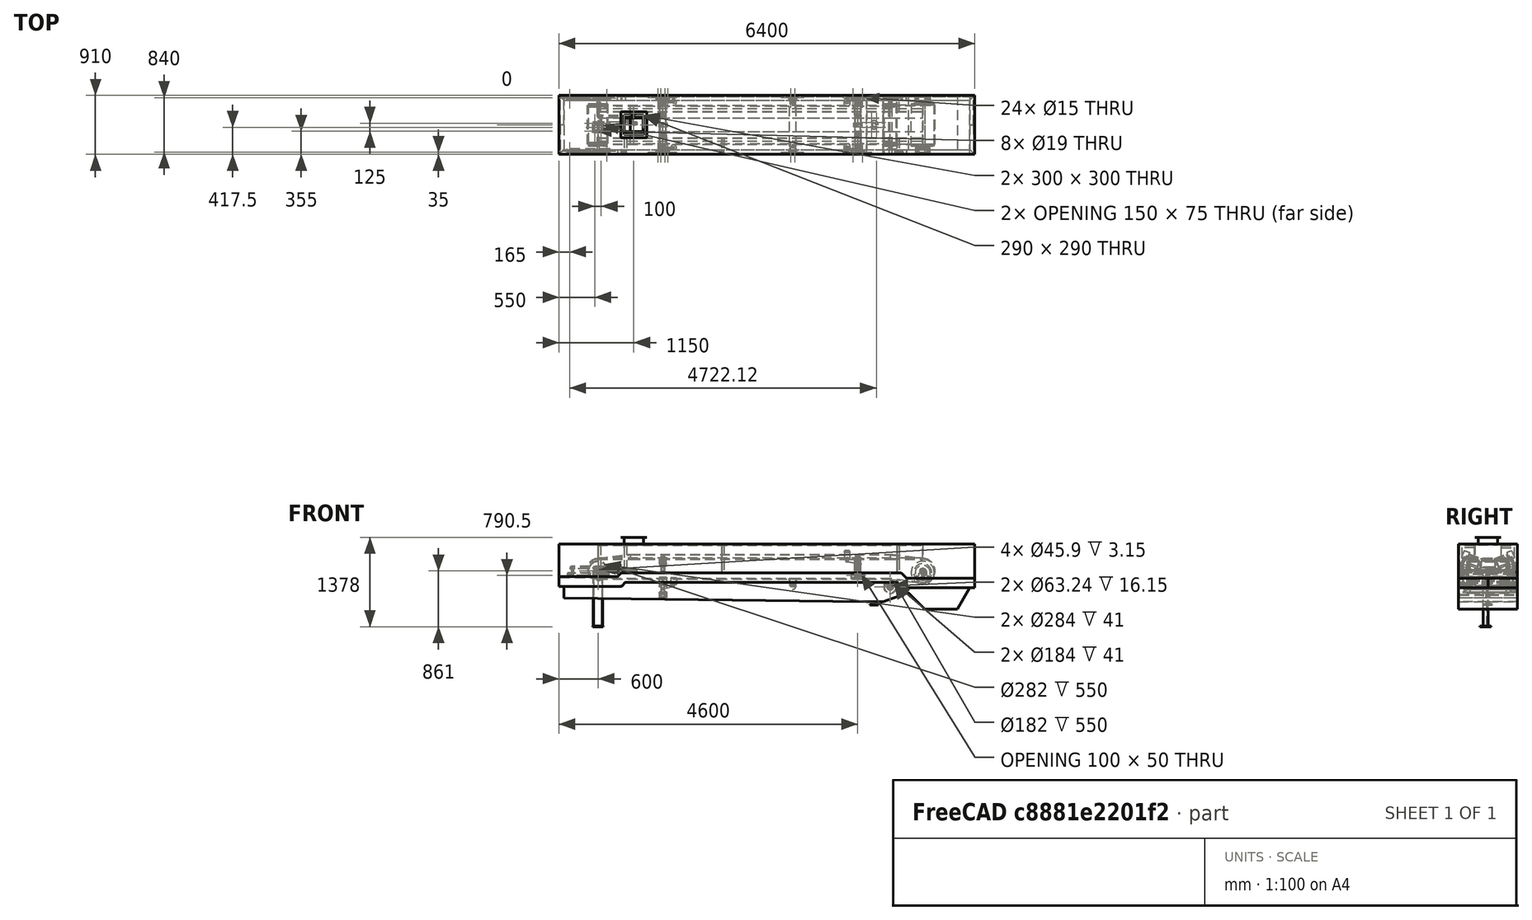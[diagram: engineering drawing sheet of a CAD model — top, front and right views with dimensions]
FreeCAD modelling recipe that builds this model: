
FCSTD DOCUMENT  (FreeCAD 0.21R33771 (Git))
Label: BeltCv600BAssy
License: All rights reserved
LicenseURL: http://en.wikipedia.org/wiki/All_rights_reserved
objects: Sketcher::SketchObject×23, Part::Extrusion×18, App::Part×18, Part::FeaturePython×15, Part::MultiFuse×10, Part::Feature×9, Part::Sweep×5, Part::Mirroring×4, Part::Thickness×3, Spreadsheet::Sheet×2, Part::Cut×2, Part::Compound×1, TechDraw::DrawSVGTemplate×1, TechDraw::DrawViewPart×1, TechDraw::DrawViewDimension×1, TechDraw::DrawPage×1
note: 89 computed .brp shape members not serialized (recipe doc carries the construction recipe); baked Part::Feature solids carry a one-line shape summary decoded from their .brp

FEATURE [Spreadsheet::Sheet] Spreadsheet
  cells = C1='tailPulleyHIght Ht; D1='Inclination k(degree); A2='CenterDistance C0; B2(C0)=5000; C2(Ht)=1000; D2(k)=10; A3='BeltWidth B0; B3(B0)=600; C3=400; D3=450; E3=500; F3=600; G3=700; H3=750; I3=800; J3=900; K3=1000; A4='Belt b1; B4(b1)=210; C4=145; D4=165; E4=180; F4=210; G4=250; H4=265; I4=280; J4=315; K4=345; A5='Belt b2; B5(b2)=195; C5==(C3 - C4) / 2; D5==(D3 - D4) / 2; E5==(E3 - E4) / 2; F5==(F3 - F4) / 2; G5==(G3 - G4) / 2; H5==(H3 - H4) / 2; I5==(I3 - I4) / 2; J5==(J3 - J4) / 2; K5==(K3 - K4) / 2; A6='BeltThickness t0; B6(t0)=10; C6=10; D6=10; E6=10; F6=10; G6=10; H6=10; I6=10; J6=10; K6=10; A7='HeadPullyDia D0; B7(D0)=360; C7=300; D7=300; E7=360; F7=360; G7=360; H7=460; I7=460; J7=520; K7=520; A8='TailPullyDia d1; B8(d1)=300; C8=260; D8=260; E8=300; F8=300; G8=300; H8=390; I8=390; J8=440; K8=440; A9='SnapPullyDia d2; B9(d2)=200; C9=200; D9=200; E9=200; F9=200; G9=200; H9=200; I9=200; J9=200; K9=200; A10='SnapPully Ls; B10(Ls)=500; C10=400; D10=400; E10=400; F10=500; G10=500; H10=500; I10=500; J10=500; K10=500; A11='SnapPully h0; B11(h0)=180; C11=180; D11=180; E11=160; F11=180; G11=180; H11=180; I11=180; J11=180; K11=180; A12='hontaihaba W; B12=910; C12=710; D12=760; E12=810; F12=910; G12=910; H12=910; I12=910; J12=910; K12=910; A13='hontai _h; B13=103.5; C13=103.5; D13=103.5; E13=103.5; F13=103.5; G13=103.5; H13=103.5; I13=103.5; J13=103.5; K13=103.5; A14='hontai_z; B14=16; C14=16; D14=16; E14=16; F14=16; G14=16; H14=16; I14=16; J14=16; K14=16; A15='takeup_x; B15=-403.47; C15=-403.47; D15=-403.47; E15=-403.47; F15=-403.47; G15=-403.47; H15=-403.47; I15=-403.47; J15=-403.47; K15=-403.47; A16='takeup_y; B16=-410; C16=-362.8; D16=-362.8; E16=-362.8; F16=-410; G16=-410; H16=-410; I16=-410; J16=-410; K16=-410; A17='takeup_z; B17=-57; C17=-87; D17=-87; E17=-87; F17=-57; G17=-57; H17=-57; I17=-57; J17=-57; K17=-57; A18='carrierPitch  cp; B18=1000; A19='returnPitch rp; B19=1500
FEATURE [Part::FeaturePython] CPM2_4145  # WARN: FeaturePython — macro-defined, semantics opaque (R4)
  A = 650
  B1 = 500
  B2 = 600
  C = 70
  D = 360
  D1 = 356
  D2 = 228
  D3 = 278
  E = 170
  F = 0
  G1 = 30
  G2 = 30
  H = 33
  L = 863
  M = 210
  N1 = 60
  N2 = 60
  P = 75
  Placement = pos=(5000,0,-30) rot=(0,0,1;1.5708rad)
  R = 20
  a = 11
  b = 11
  d = 18
  key = 5
  expr: .Placement.Base.x = Spreadsheet.C0
FEATURE [Sketcher::SketchObject] Sketch007
  FullyConstrained = true
  MapMode = 5
  Placement = pos=(0,0,14) rot=(1,0,0;1.5708rad)
  expr: Constraints[11] = Spreadsheet.C0 + 1000
  sketch-geometry (5):
    g0: LineSegment StartX=-600 StartY=-99 StartZ=0 EndX=250 EndY=-99 EndZ=0
    g1: LineSegment StartX=250 StartY=-99 StartZ=0 EndX=309 EndY=-40 EndZ=0
    g2: LineSegment StartX=309 StartY=-40 StartZ=0 EndX=4728 EndY=-40 EndZ=0
    g3: LineSegment StartX=4728 StartY=-40 StartZ=0 EndX=4800 EndY=-112 EndZ=0
    g4: LineSegment StartX=4800 StartY=-112 StartZ=0 EndX=6000 EndY=-112 EndZ=0
  constraints (16):
    c: Horizontal(g0)
    c: Coincident(g0,g1)
    c: Coincident(g1,g2)
    c: Horizontal(g2)
    c: Coincident(g2,g3)
    c: Coincident(g3,g4)
    c: Horizontal(g4)
    c: DistanceX(g0,g-1) = 600
    c: Angle(g1,g0) = 2.35619
    c: DistanceX(g-1,g0) = 250
    c: Angle(g4,g3) = 2.35619
    c: DistanceX(g-1,g4) = 6000
    c: DistanceX(g4,g4) = 1200
    c: DistanceY(g0,g-1) = 99
    c: DistanceY(g0,g1) = 59
    c: DistanceY(g-1,g3) = -112
FEATURE [Part::Feature] ChannelSteel001
  Placement = pos=(-600,-2.2e-14,-239) rot=(0,0,1;0rad)
  shape: bbox 2e-07 x 75 x 150 mm, 0 faces, 0 solids (baked)
FEATURE [Part::Feature] Carrier_600
  Placement = pos=(1000,-445,15) rot=(0,0,1;1.5708rad)
  shape: bbox 200 x 890 x 266 mm, 116 faces, 3 solids (baked)
FEATURE [Part::FeaturePython] Array  label="carrier"  # Draft array (typed FeaturePython)
  AlwaysSyncPlacement = false
  Angle = 360
  ArrayType = 0
  Axis = (0,0,1)
  Base = -> Carrier_600
  Center = (0,0,0)
  Count = 3
  ExpandArray = false
  Fuse = false
  IntervalAxis = (0,0,0)
  IntervalX = (1000,0,0)
  IntervalY = (0,100,0)
  IntervalZ = (0,0,100)
  NumberCircles = 3
  NumberPolar = 5
  NumberX = 3
  NumberY = 1
  NumberZ = 1
  PlacementList = 3 placements: arithmetic series from (1000,-445,15) step (1000,0,0) to (3000,-445,15)
  RadialDistance = 50
  ScaleList = (3) [(1,1,1),(1,1,1),(1,1,1)]
  Symmetry = 1
  TangentialDistance = 25
  expr: NumberX = Spreadsheet.C0 / Spreadsheet.B18 - 2
FEATURE [Part::FeaturePython] BendPulley  # WARN: FeaturePython — macro-defined, semantics opaque (R4)
  A = 50
  B = 103.5
  C = 700
  D = 200
  E = 0
  L = 650
  Placement = pos=(4500,1.79e-13,-250.18) rot=(0,0,-1;1.5708rad)
  d1 = 50
  d2 = 45
  d3 = 0
  t1 = 9
  t2 = 9
  t3 = 8
  t4 = 8
  expr: .Placement.Base.x = Spreadsheet.C0 - 500
FEATURE [Part::Feature] Part__Feature003  label="UCP208FC"
  Placement = pos=(4500,-410.5,-250.18) rot=(0,0.707107,-0.707107;3.14159rad)
  shape: bbox 184 x 86 x 106.1 mm, 117 faces (baked)
  expr: .Placement.Base.x = Spreadsheet.C0 - 500
FEATURE [Part::Feature] Self_Aligning_Carrier_600
  Placement = pos=(4000,1.108e-12,-38) rot=(0,0,-1;1.5708rad)
  shape: bbox 308 x 890 x 416.2 mm, 193 faces, 4 solids (baked)
  expr: .Placement.Base.x = Spreadsheet.C0 - 1000
FEATURE [Part::Feature] Self_Aligning_Return_600
  Placement = pos=(1000,0,-210) rot=(0,0,1;1.5708rad)
  shape: bbox 268 x 890 x 310 mm, 134 faces, 5 solids (baked)
FEATURE [Part::Feature] Return_600
  Placement = pos=(3000,7.84e-13,-234) rot=(0,0,1;1.5708rad)
  shape: bbox 110 x 890 x 159.5 mm, 37 faces (baked)
FEATURE [Part::FeaturePython] Array001  label="returnArray"  # Draft array (typed FeaturePython)
  AlwaysSyncPlacement = false
  Angle = 360
  ArrayType = 0
  Axis = (0,0,1)
  Base = -> Return_600
  Center = (0,0,0)
  Count = 1
  ExpandArray = false
  Fuse = false
  IntervalAxis = (0,0,0)
  IntervalX = (2000,0,0)
  IntervalY = (0,100,0)
  IntervalZ = (0,0,100)
  NumberCircles = 3
  NumberPolar = 5
  NumberX = 1
  NumberY = 1
  NumberZ = 1
  Placement = pos=(0,0,14) rot=(0,0,1;0rad)
  PlacementList = 1 placements: [(3000,7.84e-13,-234)]
  RadialDistance = 50
  ScaleList = (1) [(1,1,1)]
  Symmetry = 1
  TangentialDistance = 25
  expr: NumberX = (Spreadsheet.C0 - 3000) / 2000
FEATURE [Sketcher::SketchObject] Sketch010
  FullyConstrained = true
  MapMode = 5
  Placement = pos=(-105.6,-410.5,-87) rot=(1,0,0;3.14159rad)
FEATURE [Sketcher::SketchObject] Sketch011
  FullyConstrained = true
  MapMode = 5
  Placement = pos=(0,0,0) rot=(1,0,0;1.5708rad)
  expr: Constraints[14] = Spreadsheet.C0
  sketch-geometry (6):
    g0: LineSegment StartX=-600 StartY=-89 StartZ=0 EndX=300 EndY=-89 EndZ=0
    g1: LineSegment StartX=300 StartY=-89 StartZ=0 EndX=360 EndY=-29 EndZ=0
    g2: LineSegment StartX=360 StartY=-29 StartZ=0 EndX=4667 EndY=-29 EndZ=0
    g3: LineSegment StartX=4667 StartY=-29 StartZ=0 EndX=4750 EndY=-112 EndZ=0
    g4: LineSegment StartX=4750 StartY=-112 StartZ=0 EndX=5800 EndY=-112 EndZ=0
    g5: LineSegment StartX=7e-16 StartY=0 StartZ=0 EndX=5000 EndY=7e-16 EndZ=0
  constraints (19):
    c: Horizontal(g0)
    c: Coincident(g0,g1)
    c: Coincident(g1,g2)
    c: Horizontal(g2)
    c: Coincident(g2,g3)
    c: Coincident(g3,g4)
    c: Horizontal(g4)
    c: DistanceX(g0,g-1) = 600
    c: DistanceX(g-1,g0) = 300
    c: Angle(g1,g0) = 2.35619
    c: Angle(g4,g3) = 2.35619
    c: PointOnObject(g5,g-1)
    c: Coincident(g5,g-1)
    c: Distance(g5,g4) = 112
    c: DistanceX(g5,g5) = 5000
    c: DistanceX(g5,g4) = 800
    c: DistanceX(g3,g5) = 250
    c: DistanceY(g0,g1) = 60
    c: DistanceY(g-1,g0) = -89
FEATURE [Part::Sweep] Sweep001
  Frenet = false
  Placement = pos=(0,-455,0) rot=(0,0,1;0rad)
  Sections = -> [ChannelSteel001]
  Solid = true
  Spine = -> Sketch011 [Edge1,Edge2,Edge3,Edge4,Edge5]
  Transition = 1
FEATURE [Sketcher::SketchObject] Sketch012
  FullyConstrained = true
  MapMode = 5
  Placement = pos=(0,-455,-89) rot=(0,0,1;0rad)
  Support = -> [Sweep001]
  sketch-geometry (4):
    g0: LineSegment StartX=-480 StartY=8 StartZ=0 EndX=185 EndY=8 EndZ=0
    g1: LineSegment StartX=185 StartY=8 StartZ=0 EndX=185 EndY=83 EndZ=0
    g2: LineSegment StartX=185 StartY=83 StartZ=0 EndX=-480 EndY=83 EndZ=0
    g3: LineSegment StartX=-480 StartY=83 StartZ=0 EndX=-480 EndY=8 EndZ=0
  constraints (12):
    c: Coincident(g0,g1)
    c: Coincident(g1,g2)
    c: Coincident(g2,g3)
    c: Coincident(g3,g0)
    c: Horizontal(g0)
    c: Horizontal(g2)
    c: Vertical(g1)
    c: Vertical(g3)
    c: DistanceY(g1,g1) = 75
    c: DistanceY(g-1,g0) = 8
    c: DistanceX(g-1,g0) = 185
    c: DistanceX(g0,g0) = 665
FEATURE [Sketcher::SketchObject] Sketch013
  FullyConstrained = false
  MapMode = 5
  Placement = pos=(0,-455,-112) rot=(0,0,1;0rad)
  Support = -> [Sweep001]
  expr: Constraints[9] = Spreadsheet.C0
  sketch-geometry (5):
    g0: LineSegment StartX=4885 StartY=16.2326 StartZ=0 EndX=5115 EndY=16.2326 EndZ=0
    g1: LineSegment StartX=5115 StartY=16.2326 StartZ=0 EndX=5115 EndY=96.2326 EndZ=0
    g2: LineSegment StartX=5115 StartY=96.2326 StartZ=0 EndX=4885 EndY=96.2326 EndZ=0
    g3: LineSegment StartX=4885 StartY=96.2326 StartZ=0 EndX=4885 EndY=16.2326 EndZ=0
    g4: LineSegment StartX=5000 StartY=284.577 StartZ=0 EndX=5000 EndY=-153.677 EndZ=0
  constraints (13):
    c: Coincident(g0,g1)
    c: Coincident(g1,g2)
    c: Coincident(g2,g3)
    c: Coincident(g3,g0)
    c: Horizontal(g0)
    c: Horizontal(g2)
    c: Vertical(g1)
    c: Vertical(g3)
    c: Vertical(g4)
    c: DistanceX(g-2,g4) = 5000
    c: DistanceY(g1,g1) = 80
    c: DistanceX(g0,g0) = 230
    c: DistanceX(g4,g0) = 115
FEATURE [Part::Extrusion] Extrude004
  Base = -> Sketch013
  Dir = (0,0,1)
  DirMode = 2
  FaceMakerClass = Part::FaceMakerBullseye
  LengthFwd = 12
  LengthRev = 0
  Solid = true
  Symmetric = false
FEATURE [Sketcher::SketchObject] Sketch014
  FullyConstrained = false
  MapMode = 5
  Placement = pos=(0,-455,-179) rot=(1,0,0;3.14159rad)
  Support = -> [Sweep001]
  expr: Constraints[13] = Spreadsheet.C0 - 500
  sketch-geometry (5):
    g0: LineSegment StartX=4400 StartY=-9 StartZ=0 EndX=4600 EndY=-9 EndZ=0
    g1: LineSegment StartX=4600 StartY=-9 StartZ=0 EndX=4600 EndY=-79 EndZ=0
    g2: LineSegment StartX=4600 StartY=-79 StartZ=0 EndX=4400 EndY=-79 EndZ=0
    g3: LineSegment StartX=4400 StartY=-79 StartZ=0 EndX=4400 EndY=-9 EndZ=0
    g4: LineSegment StartX=4500 StartY=33.7597 StartZ=0 EndX=4500 EndY=-194.785 EndZ=0
  constraints (14):
    c: Coincident(g0,g1)
    c: Coincident(g1,g2)
    c: Coincident(g2,g3)
    c: Coincident(g3,g0)
    c: Horizontal(g0)
    c: Horizontal(g2)
    c: Vertical(g1)
    c: Vertical(g3)
    c: Vertical(g4)
    c: DistanceX(g0,g0) = 200
    c: DistanceY(g3,g3) = 70
    c: DistanceX(g4,g0) = 100
    c: DistanceY(g-1,g0) = -9
    c: DistanceX(g-1,g4) = 4500
FEATURE [Part::Extrusion] Extrude005
  Base = -> Sketch014
  Dir = (0,0,-1)
  DirMode = 2
  FaceMakerClass = Part::FaceMakerBullseye
  LengthFwd = 30
  LengthRev = 0
  Solid = true
  Symmetric = false
FEATURE [Part::FeaturePython] ChannelSteel  # WARN: FeaturePython — macro-defined, semantics opaque (R4)
  B = 75
  H = 150
  L = 1000
  Placement = pos=(-600,0,-239) rot=(0,0,1;0rad)
  Solid = false
  g0 = 7.85
  mass = 0
  size = 3
  standard = SS
  t1 = 6.5
  t2 = 10
FEATURE [Part::Extrusion] Extrude006
  Base = -> ChannelSteel
  Dir = (0,1,0)
  DirMode = 2
  FaceMakerClass = Part::FaceMakerBullseye
  LengthFwd = 455
  LengthRev = 0
  Reversed = true
  Solid = false
  Symmetric = false
  expr: LengthFwd = Spreadsheet.B12 / 2
FEATURE [Part::FeaturePython] ChannelSteel002  # WARN: FeaturePython — macro-defined, semantics opaque (R4)
  B = 75
  H = 150
  L = 1000
  Placement = pos=(5800,0,-112) rot=(0,1,0;3.14159rad)
  Solid = false
  g0 = 7.85
  mass = 0
  size = 3
  standard = SS
  t1 = 6.5
  t2 = 10
  expr: .Placement.Base.x = Spreadsheet.C0 + 800
FEATURE [Part::Extrusion] Extrude007
  Base = -> ChannelSteel002
  Dir = (0,1,0)
  DirMode = 2
  FaceMakerClass = Part::FaceMakerBullseye
  LengthFwd = 455
  LengthRev = 0
  Reversed = true
  Solid = false
  Symmetric = false
FEATURE [Part::Mirroring] Part__Mirroring001  label="UCP208FC (Mirror #3)"
  Base = (0,0,0)
  Normal = (0,1,0)
  Source = -> Part__Feature003
FEATURE [Part::MultiFuse] Fusion
  Refine = true
  Shapes = -> [Sweep001,Extrude006]
FEATURE [Part::Extrusion] Extrude003
  Base = -> Sketch012
  Dir = (0,0,1)
  DirMode = 2
  FaceMakerClass = Part::FaceMakerBullseye
  LengthFwd = 12
  LengthRev = 0
  Solid = true
  Symmetric = false
FEATURE [Part::MultiFuse] Fusion001
  Shapes = -> [Fusion,Extrude003]
FEATURE [Part::MultiFuse] Fusion002
  Refine = true
  Shapes = -> [Fusion001,Extrude007]
FEATURE [Part::MultiFuse] Fusion003
  Shapes = -> [Fusion002,Extrude004]
FEATURE [Part::MultiFuse] Fusion004
  Refine = true
  Shapes = -> [Fusion003,Extrude005]
FEATURE [App::Part] Part  label="本体"
  Group = -> [Fusion,ChannelSteel002,ChannelSteel,ChannelSteel001,Sweep001,Sketch011,Sketch012,Extrude005,Extrude006,Extrude003,Extrude007,Extrude004,Sketch013,Sketch014,Fusion002,Fusion003,Fusion001,Fusion004]
  Origin = -> Origin006
FEATURE [Part::Mirroring] Mirror  label="本体 (mirrored)"
  Base = (-1000,0,0)
  Normal = (0,-1,0)
  Source = -> Part
FEATURE [Part::Feature] Part__Feature  label="UCT204-Nipple"
  Placement = pos=(402.082,85.3824,0) rot=(0.519988,-0.677661,0.519988;1.95044rad)
  shape: bbox 18.99 x 12.27 x 15.73 mm, 44 faces (baked)
FEATURE [Part::Feature] Part__Feature001  label="UCT204-Housing2"
  Placement = pos=(435,77,0) rot=(0,0,1;0rad)
  shape: bbox 145.2 x 120 x 60 mm, 83 faces (baked)
FEATURE [Part::Feature] Part__Feature002  label="UCTL204-300-Frame"
  Placement = pos=(285,77,0) rot=(0,0,1;0rad)
  shape: bbox 630 x 146 x 56.5 mm, 312 faces (baked)
FEATURE [App::Part] UCTL204J_300_0  label="UCTL204J-300-0"
  Group = -> [Part__Feature,Part__Feature001,Part__Feature002]
  Origin = -> Origin008
FEATURE [App::Part] _______________________________20_v1  label="テークアップユニット_20 v1"
  Group = -> [UCTL204J_300_0]
  Origin = -> Origin001
  Placement = pos=(-435,-410,-77) rot=(1,0,0;1.5708rad)
  expr: .Placement.Base.y = -Spreadsheet001.Y
FEATURE [Part::FeaturePython] Take_upPulley001  # WARN: FeaturePython — macro-defined, semantics opaque (R4)
  A = 50
  B = 50
  C = 768
  D = 300
  E = 0
  L = 650
  Placement = pos=(0,0,0) rot=(0,0,-1;1.5708rad)
  d1 = 30
  d2 = 20
  d3 = 0
  t1 = 9
  t2 = 9
  t3 = 8
  t4 = 8
FEATURE [Sketcher::SketchObject] Sketch015
  FullyConstrained = true
  sketch-geometry (10):
    g0: LineSegment StartX=-600 StartY=-625 StartZ=0 EndX=-600 EndY=625 EndZ=0
    g1: LineSegment StartX=-600 StartY=625 StartZ=0 EndX=600 EndY=625 EndZ=0
    g2: LineSegment StartX=600 StartY=625 StartZ=0 EndX=600 EndY=-625 EndZ=0
    g3: LineSegment StartX=600 StartY=-625 StartZ=0 EndX=-600 EndY=-625 EndZ=0
    g4: GeomPoint X=0 Y=0 Z=0
    g5: LineSegment StartX=-525 StartY=-550 StartZ=0 EndX=-525 EndY=550 EndZ=0
    g6: LineSegment StartX=-525 StartY=550 StartZ=0 EndX=525 EndY=550 EndZ=0
    g7: LineSegment StartX=525 StartY=550 StartZ=0 EndX=525 EndY=-550 EndZ=0
    g8: LineSegment StartX=525 StartY=-550 StartZ=0 EndX=-525 EndY=-550 EndZ=0
    g9: GeomPoint X=0 Y=0 Z=0
  constraints (24):
    c: Coincident(g0,g1)
    c: Coincident(g1,g2)
    c: Coincident(g2,g3)
    c: Coincident(g3,g0)
    c: Horizontal(g1)
    c: Horizontal(g3)
    c: Vertical(g0)
    c: Vertical(g2)
    c: Symmetric(g1,g0,g4)
    c: Coincident(g4,g-1)
    c: Distance(g0) = 1250
    c: Distance(g4,g0) = 600
    c: Coincident(g5,g6)
    c: Coincident(g6,g7)
    c: Coincident(g7,g8)
    c: Coincident(g8,g5)
    c: Horizontal(g6)
    c: Horizontal(g8)
    c: Vertical(g5)
    c: Vertical(g7)
    c: Symmetric(g6,g5,g9)
    c: Coincident(g9,g4)
    c: Distance(g5,g0) = 75
    c: Distance(g5,g1) = 75
FEATURE [Part::Mirroring] Mirror001  label="テークアップユニット_20 v1 (mirrored)"
  Base = (-400,0,0)
  Normal = (0,-1,0)
  Source = -> _______________________________20_v1
FEATURE [Part::Compound] Compound  label="takeUp"
  Links = -> [Mirror001,_______________________________20_v1]
FEATURE [App::Part] Part004  label="pulley"
  Group = -> [Take_upPulley001]
  Origin = -> Origin003
  Placement = pos=(0,0,0) rot=(0,1,0;2.1293rad)
FEATURE [Spreadsheet::Sheet] Spreadsheet001  label="Spreadsheet_takeup"
  cells = A1='beltWidth; B1='takeup d0; C1='d1=d0+10; D1='pulley D0; E1='puller L0; F1='puller C0; G1='puller B0; H1='takeup Y; A2(W0)=600; B2(d0)=20; C2(d1)==d0 + 10; D2(D0)=300; E2(L0)=650; F2(C0)=768; G2(B0)=50; H2(Y)=410; A3=400; B3=20; C3==d0 + 10; D3=300; E3=450; F3=568; G3=50; H3=310; A4=450; B4=20; C4==d0 + 10; D4=300; E4=500; F4=618; G4=50; H4=335; A5=500; B5=20; C5==d0 + 10; D5=300; E5=550; F5=668; G5=50; H5=360; A6=600; B6=20; C6==d0 + 10; D6=300; E6=650; F6=768; G6=50; H6=410; A7=700; B7=20; C7==d0 + 10; D7=300; E7=750; F7=868; G7=50; H7=460; A8=750; B8=20; C8==d0 + 10; D8=300; E8=800; F8=918; G8=50; H8=485; A9=800; B9=20; C9==d0 + 10; D9=300; E9=850; F9=968; G9=50; H9=510; A10=900; B10=20; C10==d0 + 10; D10=300; E10=950; F10=1068; G10=50; H10=560; A11=1000; B11=20; C11==d0 + 10; D11=300; E11=1050; F11=1168; G11=50; H11=610
FEATURE [App::Part] Part003  label="takeUpAssy20d"
  Group = -> [_______________________________20_v1,Mirror001,Compound,Sketch015,Part004,Spreadsheet001]
  Origin = -> Origin002
FEATURE [App::Part] Part005  label="bendPulley"
  Group = -> [BendPulley,Part__Feature003,Part__Mirroring001]
  Origin = -> Origin009
  Placement = pos=(0,0,-8) rot=(0,0,1;0rad)
FEATURE [Sketcher::SketchObject] Sketch016
  FullyConstrained = true
  Placement = pos=(0,0,0) rot=(0.57735,0.57735,0.57735;2.0944rad)
  sketch-geometry (6):
    g0: LineSegment StartX=200 StartY=200 StartZ=0 EndX=206 EndY=200 EndZ=0
    g1: LineSegment StartX=206 StartY=200 StartZ=0 EndX=206 EndY=394 EndZ=0
    g2: LineSegment StartX=200 StartY=400 StartZ=0 EndX=200 EndY=200 EndZ=0
    g3: LineSegment StartX=250 StartY=400 StartZ=0 EndX=250 EndY=394 EndZ=0
    g4: LineSegment StartX=250 StartY=394 StartZ=0 EndX=206 EndY=394 EndZ=0
    g5: LineSegment StartX=200 StartY=400 StartZ=0 EndX=250 EndY=400 EndZ=0
  constraints (18):
    c: Coincident(g0,g1)
    c: Coincident(g2,g0)
    c: Horizontal(g0)
    c: Vertical(g1)
    c: Vertical(g2)
    c: DistanceX(g-2,g2) = 200
    c: Vertical(g3)
    c: Coincident(g3,g4)
    c: Horizontal(g4)
    c: Coincident(g1,g4)
    c: Coincident(g5,g2)
    c: Coincident(g5,g3)
    c: Horizontal(g5)
    c: DistanceY(g3,g3) = 6
    c: DistanceX(g5,g5) = 50
    c: DistanceY(g2,g2) = 200
    c: DistanceX(g0,g0) = 6
    c: DistanceY(g-1,g2) = 400
FEATURE [Part::Extrusion] Extrude010
  Base = -> Sketch016
  Dir = (1,0,0)
  DirMode = 2
  FaceMakerClass = Part::FaceMakerBullseye
  LengthFwd = 5000
  LengthRev = 0
  Solid = true
  Symmetric = false
  expr: LengthFwd = Spreadsheet.C0
FEATURE [Sketcher::SketchObject] Sketch017
  FullyConstrained = false
  Placement = pos=(0,0,0) rot=(0.57735,0.57735,0.57735;2.0944rad)
  sketch-geometry (2):
    g0: LineSegment StartX=205.947 StartY=393.774 StartZ=0 EndX=443.566 EndY=393.774 EndZ=0
    g1: LineSegment StartX=443.566 StartY=393.774 StartZ=0 EndX=443.566 EndY=-26.5991 EndZ=0
  constraints (3):
    c: Horizontal(g0)
    c: Vertical(g1)
    c: Coincident(g1,g0)
FEATURE [Part::FeaturePython] AngleSteel  # WARN: FeaturePython — macro-defined, semantics opaque (R4)
  A = 40
  B = 40
  L = 1000
  Placement = pos=(0,223.3,394) rot=(1,0,0;3.14159rad)
  Solid = false
  g0 = 7.85
  mass = 0
  size = 5
  standard = SS_Equal
  t = 5
FEATURE [Part::Sweep] Sweep002
  Frenet = false
  Sections = -> [AngleSteel]
  Solid = true
  Spine = -> Sketch017 [Edge1,Edge2]
  Transition = 1
FEATURE [Sketcher::SketchObject] Sketch018
  FullyConstrained = false
  MapMode = 5
  Placement = pos=(3e-16,-1.6e-15,-26.5991) rot=(1,0,0;3.14159rad)
  Support = -> [Sweep002]
  sketch-geometry (4):
    g0: LineSegment StartX=-30 StartY=-443.912 StartZ=0 EndX=40.1109 EndY=-443.912 EndZ=0
    g1: LineSegment StartX=40.1109 StartY=-443.912 StartZ=0 EndX=40.1109 EndY=-403.912 EndZ=0
    g2: LineSegment StartX=40.1109 StartY=-403.912 StartZ=0 EndX=-30 EndY=-403.912 EndZ=0
    g3: LineSegment StartX=-30 StartY=-403.912 StartZ=0 EndX=-30 EndY=-443.912 EndZ=0
  constraints (10):
    c: Coincident(g0,g1)
    c: Coincident(g1,g2)
    c: Coincident(g2,g3)
    c: Coincident(g3,g0)
    c: Horizontal(g0)
    c: Horizontal(g2)
    c: Vertical(g1)
    c: Vertical(g3)
    c: DistanceY(g3,g3) = 40
    c: DistanceX(g-2,g0) = -30
FEATURE [Part::Extrusion] Extrude011
  Base = -> Sketch018
  Dir = (0,-1e-16,-1)
  DirMode = 2
  FaceMakerClass = Part::FaceMakerBullseye
  LengthFwd = 6
  LengthRev = 0
  Reversed = true
  Solid = true
  Symmetric = false
FEATURE [App::Part] Part009  label="post001"
  Group = -> [Sketch017,Sweep002,AngleSteel,Extrude011,Sketch018]
  Origin = -> Origin013
  Placement = pos=(400,0,0) rot=(0,0,1;0rad)
FEATURE [Part::FeaturePython] Clone001  label="post002"  # Draft clone (typed FeaturePython)
  AttacherType = Attacher::AttachEngine3D
  Fuse = false
  Objects = -> [Part009]
  Placement = pos=(4600,0,0) rot=(0,0,1;0rad)
  Scale = (1,1,1)
  expr: .Placement.Base.x = Spreadsheet.C0 - 400
FEATURE [Part::FeaturePython] Array003  # Draft array (typed FeaturePython)
  AlwaysSyncPlacement = false
  Angle = 360
  ArrayType = 0
  Axis = (0,0,1)
  Base = -> Part009
  Center = (0,0,0)
  Count = 2
  ExpandArray = false
  Fuse = false
  IntervalAxis = (0,0,0)
  IntervalX = (1500,0,0)
  IntervalY = (0,100,0)
  IntervalZ = (0,0,100)
  NumberCircles = 3
  NumberPolar = 5
  NumberX = 2
  NumberY = 1
  NumberZ = 1
  PlacementList = 2 placements: [(400,0,0),(1900,0,0)]
  RadialDistance = 50
  ScaleList = (2) [(1,1,1),(1,1,1)]
  Symmetry = 1
  TangentialDistance = 25
  expr: NumberX = Spreadsheet.C0 / 1500 - 1
FEATURE [App::Part] Part008  label="skirt"
  Group = -> [Sketch016,Extrude010,Part009,Clone001,Array003]
  Origin = -> Origin012
FEATURE [Part::Mirroring] Mirror003  label="skirt001"
  Base = (-900,0,0)
  Normal = (0,-1,0)
  Source = -> Part008
FEATURE [App::Part] Part010  label="Pulleys"
  Group = -> [Return_600,Array001,Self_Aligning_Return_600,Self_Aligning_Carrier_600,Carrier_600,Array,Part005,Part003,CPM2_4145]
  Origin = -> Origin014
FEATURE [App::Part] Part011  label="Skirt"
  Group = -> [Part008,Mirror003]
  Origin = -> Origin015
FEATURE [App::Part] Part012  label="Frame"
  Group = -> [Part,Mirror,Sketch007,Sketch010]
  Origin = -> Origin016
FEATURE [Sketcher::SketchObject] Sketch020
  FullyConstrained = true
  Placement = pos=(0,0,0) rot=(1,0,0;1.5708rad)
  expr: Constraints[19] = Spreadsheet.C0 + 1400
  sketch-geometry (8):
    g0: LineSegment StartX=-600 StartY=-89 StartZ=0 EndX=-600 EndY=411 EndZ=0
    g1: LineSegment StartX=-600 StartY=411 StartZ=0 EndX=5800 EndY=411 EndZ=0
    g2: LineSegment StartX=5800 StartY=411 StartZ=0 EndX=5800 EndY=-112 EndZ=0
    g3: LineSegment StartX=5800 StartY=-112 StartZ=0 EndX=4750 EndY=-112 EndZ=0
    g4: LineSegment StartX=4750 StartY=-112 StartZ=0 EndX=4667 EndY=-29 EndZ=0
    g5: LineSegment StartX=4667 StartY=-29 StartZ=0 EndX=360 EndY=-29 EndZ=0
    g6: LineSegment StartX=360 StartY=-29 StartZ=0 EndX=300 EndY=-89 EndZ=0
    g7: LineSegment StartX=300 StartY=-89 StartZ=0 EndX=-600 EndY=-89 EndZ=0
  constraints (24):
    c: Vertical(g0)
    c: Coincident(g0,g1)
    c: Horizontal(g1)
    c: Coincident(g1,g2)
    c: Vertical(g2)
    c: Coincident(g2,g3)
    c: Horizontal(g3)
    c: Coincident(g3,g4)
    c: Coincident(g4,g5)
    c: Horizontal(g5)
    c: Coincident(g5,g6)
    c: Coincident(g6,g7)
    c: Coincident(g7,g0)
    c: Horizontal(g7)
    c: Distance(g-1,g0) = 600
    c: Distance(g-1,g7) = 89
    c: DistanceX(g-1,g6) = 300
    c: Angle(g6,g5) = 2.35619
    c: DistanceY(g6,g5) = 60
    c: DistanceX(g1,g1) = 6400
    c: DistanceY(g-1,g2) = -112
    c: Distance(g3) = 1050
    c: Angle(g3,g4) = 2.35619
    c: DistanceY(g0,g0) = 500
FEATURE [Part::Extrusion] Extrude012
  Base = -> Sketch020
  Dir = (0,-1,2e-16)
  DirMode = 2
  FaceMakerClass = Part::FaceMakerBullseye
  LengthFwd = 910
  LengthRev = 0
  Solid = true
  Symmetric = true
FEATURE [Part::Thickness] Thickness
  Faces = -> Extrude012 [Face8,Face7,Face6,Face5,Face4]
  Intersection = true
  Join = 2
  Mode = 0
  SelfIntersection = true
  Value = -5
FEATURE [Sketcher::SketchObject] Sketch021
  FullyConstrained = true
  MapMode = 5
  Placement = pos=(0,9.13e-14,411) rot=(0,0,1;0rad)
  Support = -> [Thickness]
  sketch-geometry (4):
    g0: LineSegment StartX=400 StartY=-150 StartZ=0 EndX=700 EndY=-150 EndZ=0
    g1: LineSegment StartX=700 StartY=-150 StartZ=0 EndX=700 EndY=150 EndZ=0
    g2: LineSegment StartX=700 StartY=150 StartZ=0 EndX=400 EndY=150 EndZ=0
    g3: LineSegment StartX=400 StartY=150 StartZ=0 EndX=400 EndY=-150 EndZ=0
  constraints (12):
    c: Coincident(g0,g1)
    c: Coincident(g1,g2)
    c: Coincident(g2,g3)
    c: Coincident(g3,g0)
    c: Horizontal(g0)
    c: Horizontal(g2)
    c: Vertical(g1)
    c: Vertical(g3)
    c: DistanceX(g2,g2) = 300
    c: DistanceY(g3,g3) = 300
    c: DistanceY(g-1,g2) = 150
    c: DistanceX(g-1,g2) = 400
FEATURE [Part::Extrusion] Extrude013
  Base = -> Sketch021
  Dir = (0,2e-16,1)
  DirMode = 2
  FaceMakerClass = Part::FaceMakerBullseye
  LengthFwd = 100
  LengthRev = 10
  Solid = true
  Symmetric = false
FEATURE [Part::Cut] Cut
  Base = -> Thickness
  Tool = -> Extrude013
FEATURE [Part::Thickness] Thickness001
  Faces = -> Extrude013 [Face5,Face6]
  Intersection = false
  Join = 0
  Mode = 0
  SelfIntersection = false
  Value = -5
FEATURE [Sketcher::SketchObject] Sketch022
  ExternalGeometry = -> [Thickness001]
  FullyConstrained = true
  MapMode = 5
  Placement = pos=(0,1.936e-13,511) rot=(0,0,1;0rad)
  Support = -> [Thickness001]
  sketch-geometry (8):
    g0: LineSegment StartX=350 StartY=-200 StartZ=0 EndX=750 EndY=-200 EndZ=0
    g1: LineSegment StartX=750 StartY=-200 StartZ=0 EndX=750 EndY=200 EndZ=0
    g2: LineSegment StartX=750 StartY=200 StartZ=0 EndX=350 EndY=200 EndZ=0
    g3: LineSegment StartX=350 StartY=200 StartZ=0 EndX=350 EndY=-200 EndZ=0
    g4: LineSegment StartX=400 StartY=-150 StartZ=0 EndX=700 EndY=-150 EndZ=0
    g5: LineSegment StartX=700 StartY=-150 StartZ=0 EndX=700 EndY=150 EndZ=0
    g6: LineSegment StartX=700 StartY=150 StartZ=0 EndX=400 EndY=150 EndZ=0
    g7: LineSegment StartX=400 StartY=150 StartZ=0 EndX=400 EndY=-150 EndZ=0
  constraints (22):
    c: Coincident(g0,g1)
    c: Coincident(g1,g2)
    c: Coincident(g2,g3)
    c: Coincident(g3,g0)
    c: Horizontal(g0)
    c: Horizontal(g2)
    c: Vertical(g1)
    c: Vertical(g3)
    c: Distance(g-3,g1) = 50
    c: Distance(g-3,g2) = 50
    c: Distance(g-4,g0) = 50
    c: Distance(g-4,g3) = 50
    c: Coincident(g4,g5)
    c: Coincident(g5,g6)
    c: Coincident(g6,g7)
    c: Coincident(g7,g4)
    c: Horizontal(g4)
    c: Horizontal(g6)
    c: Vertical(g5)
    c: Vertical(g7)
    c: Coincident(g5,g-3)
    c: Coincident(g4,g-4)
FEATURE [Part::Extrusion] Extrude014
  Base = -> Sketch022
  Dir = (0,4e-16,1)
  DirMode = 2
  FaceMakerClass = Part::FaceMakerBullseye
  LengthFwd = 6
  LengthRev = 0
  Solid = true
  Symmetric = false
FEATURE [Part::MultiFuse] Fusion007
  Shapes = -> [Thickness001,Extrude014]
FEATURE [Part::MultiFuse] Fusion008
  Shapes = -> [Cut,Fusion007]
FEATURE [App::Part] Part013  label="Cover"
  Group = -> [Cut,Fusion007,Sketch022,Sketch021,Sketch020,Thickness,Thickness001,Extrude013,Extrude012,Extrude014,Fusion008]
  Origin = -> Origin017
FEATURE [Sketcher::SketchObject] Sketch023
  FullyConstrained = true
  Placement = pos=(0,0,0) rot=(1,0,0;1.5708rad)
  expr: Constraints[26] = Spreadsheet.C0 + 725
  sketch-geometry (12):
    g0: LineSegment StartX=-525 StartY=-239 StartZ=0 EndX=362.13 EndY=-239 EndZ=0
    g1: LineSegment StartX=362.13 StartY=-239 StartZ=0 EndX=422.13 EndY=-179 EndZ=0
    g2: LineSegment StartX=422.13 StartY=-179 StartZ=0 EndX=4605 EndY=-179 EndZ=0
    g3: LineSegment StartX=4605 StartY=-179 StartZ=0 EndX=4688 EndY=-262 EndZ=0
    g4: LineSegment StartX=4688 StartY=-262 StartZ=0 EndX=5725 EndY=-262 EndZ=0
    g5: LineSegment StartX=5725 StartY=-262 StartZ=0 EndX=5534.47 EndY=-592 EndZ=0
    g6: LineSegment StartX=5534.47 StartY=-592 StartZ=0 EndX=5034.47 EndY=-592 EndZ=0
    g7: LineSegment StartX=5034.47 StartY=-592 StartZ=0 EndX=4779.47 EndY=-337 EndZ=0
    g8: LineSegment StartX=4779.47 StartY=-337 StartZ=0 EndX=4389.47 EndY=-478.948 EndZ=0
    g9: LineSegment StartX=4389.47 StartY=-478.948 StartZ=0 EndX=4139.47 EndY=-478.948 EndZ=0
    g10: LineSegment StartX=4139.47 StartY=-478.948 StartZ=0 EndX=-525 EndY=-419 EndZ=0
    g11: LineSegment StartX=-525 StartY=-419 StartZ=0 EndX=-525 EndY=-239 EndZ=0
  constraints (36):
    c: Horizontal(g0)
    c: Coincident(g0,g1)
    c: Coincident(g1,g2)
    c: Horizontal(g2)
    c: Coincident(g2,g3)
    c: Coincident(g3,g4)
    c: Horizontal(g4)
    c: Coincident(g4,g5)
    c: Coincident(g5,g6)
    c: Horizontal(g6)
    c: Coincident(g6,g7)
    c: Coincident(g7,g8)
    c: Coincident(g8,g9)
    c: Horizontal(g9)
    c: Coincident(g9,g10)
    c: Coincident(g10,g11)
    c: Coincident(g11,g0)
    c: Vertical(g11)
    c: DistanceY(g11,g11) = 180
    c: DistanceX(g0,g-1) = 525
    c: DistanceY(g0,g-1) = 239
    c: DistanceX(g0,g0) = 887.13
    c: Angle(g1,g0) = 2.35619
    c: DistanceY(g-1,g2) = -179
    c: Angle(g4,g3) = 2.35619
    c: DistanceY(g-1,g3) = -262
    c: DistanceX(g-1,g4) = 5725
    c: DistanceY(g5,g4) = 330
    c: Angle(g5,g6) = 2.0944
    c: DistanceX(g6,g6) = 500
    c: Angle(g6,g7) = 2.35619
    c: DistanceY(g7,g3) = 75
    c: Angle(g8,g9) = 2.79253
    c: DistanceX(g8,g7) = 390
    c: DistanceX(g9,g9) = 250
    c: DistanceX(g4,g4) = 1037
FEATURE [Part::Extrusion] Extrude015
  Base = -> Sketch023
  Dir = (0,-1,2e-16)
  DirMode = 2
  FaceMakerClass = Part::FaceMakerBullseye
  LengthFwd = 910
  LengthRev = 0
  Solid = true
  Symmetric = true
FEATURE [Part::Thickness] Thickness002
  Faces = -> Extrude015 [Face1,Face2,Face3,Face4,Face5,Face7]
  Intersection = false
  Join = 2
  Mode = 0
  SelfIntersection = false
  Value = -3
FEATURE [Part::FeaturePython] Single_flange_straight_pipe  # WARN: FeaturePython — macro-defined, semantics opaque (R4)
  L = 50
  Placement = pos=(4250,0,-530.405) rot=(0,-1,0;1.5708rad)
  dia = 6
  fittings = 06_Single_flange_straight_pipe
  material = 0
  standard = 0
  standard2 = 0
  expr: .Placement.Base.x = Spreadsheet.C0 - 750
FEATURE [Sketcher::SketchObject] Sketch024
  FullyConstrained = false
  MapMode = 5
  Placement = pos=(0,-1.057e-13,-475.948) rot=(0,0,1;0rad)
  Support = -> [Thickness002]
  expr: Constraints[1] = Spreadsheet.C0 - 750
  sketch-geometry (1):
    g0: Circle CenterX=4250 CenterY=0 CenterZ=0 NormalX=0 NormalY=0 NormalZ=1 AngleXU=0 Radius=30.4407
  constraints (2):
    c: PointOnObject(g0,g-1)
    c: DistanceX(g-1,g0) = 4250
FEATURE [Part::Extrusion] Extrude016  label="drain"
  Base = -> Sketch024
  Dir = (0,2e-16,1)
  DirMode = 2
  FaceMakerClass = Part::FaceMakerBullseye
  LengthFwd = 10
  LengthRev = 0
  Solid = true
  Symmetric = true
FEATURE [Part::Cut] Cut001
  Base = -> Thickness002
  Tool = -> Extrude016
FEATURE [Part::MultiFuse] Fusion009
  Shapes = -> [Cut001,Single_flange_straight_pipe]
FEATURE [App::Part] Part014  label="waterReceptacle"
  Group = -> [Cut001,Sketch023,Single_flange_straight_pipe,Thickness002,Sketch024,Extrude015,Extrude016,Fusion009]
  Origin = -> Origin018
FEATURE [Sketcher::SketchObject] Sketch
  FullyConstrained = true
  Placement = pos=(0,0,0) rot=(0.57735,0.57735,0.57735;2.0944rad)
  expr: Constraints[1] = Spreadsheet.B0
  expr: Constraints[2] = Spreadsheet.D0 / 2
  sketch-geometry (1):
    g0: LineSegment StartX=-300 StartY=180 StartZ=0 EndX=300 EndY=180 EndZ=0
  constraints (3):
    c: Symmetric(g0,g0,g-2)
    c: DistanceX(g0,g0) = 600
    c: Distance(g-1,g0) = 180
FEATURE [Sketcher::SketchObject] Sketch001
  FullyConstrained = true
  Placement = pos=(5000,0,0) rot=(0.57735,0.57735,0.57735;2.0944rad)
  expr: .Placement.Base.x = Spreadsheet.C0
  expr: Constraints[1] = Spreadsheet.B0
  expr: Constraints[2] = Spreadsheet.D0 / 2
  sketch-geometry (1):
    g0: LineSegment StartX=-300 StartY=180 StartZ=0 EndX=300 EndY=180 EndZ=0
  constraints (3):
    c: Symmetric(g0,g0,g-2)
    c: DistanceX(g0,g0) = 600
    c: Distance(g-1,g0) = 180
FEATURE [Sketcher::SketchObject] Sketch002
  FullyConstrained = true
  Placement = pos=(500,0,0) rot=(0.57735,0.57735,0.57735;2.0944rad)
  expr: Constraints[5] = Spreadsheet.b2
  expr: Constraints[6] = Spreadsheet.b2
  expr: Constraints[7] = Spreadsheet.D0 / 2
  expr: Constraints[8] = Spreadsheet.b1
  sketch-geometry (3):
    g0: LineSegment StartX=-288.24 StartY=246.694 StartZ=0 EndX=-105 EndY=180 EndZ=0
    g1: LineSegment StartX=-105 StartY=180 StartZ=0 EndX=105 EndY=180 EndZ=0
    g2: LineSegment StartX=105 StartY=180 StartZ=0 EndX=288.24 EndY=246.694 EndZ=0
  constraints (9):
    c: Coincident(g0,g1)
    c: Coincident(g1,g2)
    c: Angle(g2,g1) = 2.79253
    c: Angle(g1,g0) = 2.79253
    c: Symmetric(g1,g0,g-2)
    c: Distance(g2) = 195
    c: Distance(g0) = 195
    c: DistanceY(g-1,g1) = 180
    c: DistanceX(g1,g1) = 210
FEATURE [Sketcher::SketchObject] Sketch003
  FullyConstrained = true
  Placement = pos=(4500,0,0) rot=(0.57735,0.57735,0.57735;2.0944rad)
  expr: .Placement.Base.x = Spreadsheet.C0 - 500
  expr: Constraints[5] = Spreadsheet.b2
  expr: Constraints[6] = Spreadsheet.b2
  expr: Constraints[7] = Spreadsheet.D0 / 2
  expr: Constraints[8] = Spreadsheet.b1
  sketch-geometry (3):
    g0: LineSegment StartX=-288.24 StartY=246.694 StartZ=0 EndX=-105 EndY=180 EndZ=0
    g1: LineSegment StartX=-105 StartY=180 StartZ=0 EndX=105 EndY=180 EndZ=0
    g2: LineSegment StartX=105 StartY=180 StartZ=0 EndX=288.24 EndY=246.694 EndZ=0
  constraints (9):
    c: Coincident(g0,g1)
    c: Coincident(g1,g2)
    c: Angle(g2,g1) = 2.79253
    c: Angle(g1,g0) = 2.79253
    c: Symmetric(g1,g0,g-2)
    c: Distance(g2) = 195
    c: Distance(g0) = 195
    c: DistanceY(g-1,g1) = 180
    c: DistanceX(g1,g1) = 210
FEATURE [Sketcher::SketchObject] Sketch005
  FullyConstrained = true
  Placement = pos=(5000,0,0) rot=(1,0,0;1.5708rad)
  expr: .Placement.Base.x = Spreadsheet.C0
  expr: Constraints[0] = Spreadsheet.D0
  expr: Constraints[10] = Spreadsheet.Ls
  expr: Constraints[20] = Spreadsheet.t0
  expr: Constraints[22] = Spreadsheet.t0
  expr: Constraints[29] = (Spreadsheet.D0 - Spreadsheet.d1) / 2
  expr: Constraints[2] = Spreadsheet.d1
  expr: Constraints[6] = Spreadsheet.d2 / 2
  expr: Constraints[8] = Spreadsheet.C0
  sketch-geometry (12):
    g0: ArcOfCircle CenterX=0 CenterY=0 CenterZ=0 NormalX=0 NormalY=0 NormalZ=1 AngleXU=0 Radius=180 StartAngle=4.58871 EndAngle=7.85398
    g1: ArcOfCircle CenterX=-5000 CenterY=30 CenterZ=0 NormalX=0 NormalY=0 NormalZ=1 AngleXU=0 Radius=150 StartAngle=1.5708 EndAngle=4.71239
    g2: LineSegment StartX=-22.2048 StartY=-178.625 StartZ=0 EndX=-487.664 EndY=-120.764 EndZ=0
    g3: LineSegment StartX=-500 StartY=-120 StartZ=0 EndX=-5000 EndY=-120 EndZ=0
    g4: ArcOfCircle CenterX=-500 CenterY=-220 CenterZ=0 NormalX=0 NormalY=0 NormalZ=1 AngleXU=0 Radius=100 StartAngle=1.44712 EndAngle=1.5708
    g5: ArcOfCircle CenterX=-5000 CenterY=30 CenterZ=0 NormalX=0 NormalY=0 NormalZ=1 AngleXU=0 Radius=160 StartAngle=1.5708 EndAngle=4.71239
    g6: LineSegment StartX=-5000 StartY=-130 StartZ=0 EndX=-500 EndY=-130 EndZ=0
    g7: ArcOfCircle CenterX=-500 CenterY=-220 CenterZ=0 NormalX=0 NormalY=0 NormalZ=1 AngleXU=0 Radius=90 StartAngle=1.44712 EndAngle=1.5708
    g8: LineSegment StartX=-488.898 StartY=-130.687 StartZ=0 EndX=-23.4385 EndY=-188.549 EndZ=0
    g9: ArcOfCircle CenterX=0 CenterY=0 CenterZ=0 NormalX=0 NormalY=0 NormalZ=1 AngleXU=0 Radius=190 StartAngle=4.58871 EndAngle=7.85398
    g10: LineSegment StartX=0 StartY=180 StartZ=0 EndX=5.82e-14 EndY=190 EndZ=0
    g11: LineSegment StartX=-5000 StartY=180 StartZ=0 EndX=-5000 EndY=190 EndZ=0
  constraints (32):
    c: Diameter(g0) = 360
    c: Coincident(g-1,g0)
    c: Diameter(g1) = 300
    c: Horizontal(g3)
    c: Tangent(g2,g4) = -1.5708
    c: Tangent(g3,g4) = -1.5708
    c: Radius(g4) = 100
    c: Coincident(g1,g3)
    c: DistanceX(g1,g0) = 5000
    c: Vertical(g0,g0)
    c: DistanceX(g4,g0) = 500
    c: Vertical(g1,g1)
    c: Coincident(g5,g1)
    c: Tangent(g5,g6) = -1.5708
    c: Tangent(g6,g7) = 1.5708
    c: Tangent(g8,g9) = -1.5708
    c: PointOnObject(g9,g-2)
    c: Coincident(g10,g0)
    c: Coincident(g10,g9)
    c: Coincident(g9,g0)
    c: DistanceY(g10,g10) = 10
    c: Coincident(g4,g7)
    c: DistanceY(g5,g1) = 10
    c: Vertical(g1,g5)
    c: Coincident(g11,g1)
    c: Coincident(g11,g5)
    c: Tangent(g7,g8) = 1.5708
    c: Vertical(g1,g1)
    c: Parallel(g8,g2)
    c: DistanceY(g-1,g1) = 30
    c: Parallel(g6,g3)
    c: Coincident(g2,g0)
FEATURE [Part::Extrusion] Extrude
  Base = -> Sketch005
  Dir = (0,-1,2e-16)
  DirMode = 2
  FaceMakerClass = Part::FaceMakerBullseye
  LengthFwd = 600
  LengthRev = 0
  Solid = true
  Symmetric = true
  expr: LengthFwd = Spreadsheet.B0
FEATURE [Sketcher::SketchObject] Sketch025
  FullyConstrained = true
  Placement = pos=(0,0,0) rot=(1,0,0;1.5708rad)
  sketch-geometry (1):
    g0: LineSegment StartX=0 StartY=180 StartZ=0 EndX=500 EndY=180 EndZ=0
  constraints (4):
    c: Horizontal(g0)
    c: Vertical(g0,g-1)
    c: DistanceY(g-1,g0) = 180
    c: DistanceX(g0,g0) = 500
FEATURE [Sketcher::SketchObject] Sketch008
  FullyConstrained = true
  Placement = pos=(0,0,0) rot=(1,0,0;1.5708rad)
  expr: Constraints[2] = Spreadsheet.C0
  sketch-geometry (1):
    g0: LineSegment StartX=4500 StartY=180 StartZ=0 EndX=5000 EndY=180 EndZ=0
  constraints (4):
    c: Horizontal(g0)
    c: DistanceY(g-1,g0) = 180
    c: DistanceX(g-1,g0) = 5000
    c: DistanceX(g0,g0) = 500
FEATURE [Sketcher::SketchObject] Sketch009
  FullyConstrained = true
  Placement = pos=(0,0,0) rot=(1,0,0;1.5708rad)
  sketch-geometry (1):
    g0: LineSegment StartX=500 StartY=180 StartZ=0 EndX=4500 EndY=180 EndZ=0
  constraints (4):
    c: Horizontal(g0)
    c: DistanceX(g-1,g0) = 500
    c: DistanceY(g-1,g0) = 180
    c: DistanceX(g0,g0) = 4000
FEATURE [Part::Sweep] Sweep003
  Frenet = false
  Sections = -> [Sketch002,Sketch003]
  Solid = false
  Spine = -> Sketch009 [Edge1]
  Transition = 1
FEATURE [Part::Extrusion] Extrude017
  Base = -> Sweep003
  Dir = (0,0,1)
  DirMode = 0
  FaceMakerClass = Part::FaceMakerBullseye
  LengthFwd = 10
  LengthRev = 0
  Solid = false
  Symmetric = false
FEATURE [Part::Sweep] Sweep
  Frenet = false
  Sections = -> [Sketch,Sketch002]
  Solid = false
  Spine = -> Sketch025 [Edge1]
  Transition = 1
FEATURE [Part::Extrusion] Extrude018
  Base = -> Sweep
  Dir = (0,0,1)
  DirMode = 0
  FaceMakerClass = Part::FaceMakerBullseye
  LengthFwd = 10
  LengthRev = 0
  Solid = false
  Symmetric = false
FEATURE [Part::Sweep] Sweep004
  Frenet = false
  Sections = -> [Sketch001,Sketch003]
  Solid = false
  Spine = -> Sketch008 [Edge1]
  Transition = 1
FEATURE [Part::Extrusion] Extrude019
  Base = -> Sweep004
  Dir = (0,0,1)
  DirMode = 0
  FaceMakerClass = Part::FaceMakerBullseye
  LengthFwd = 10
  LengthRev = 0
  Solid = false
  Symmetric = false
FEATURE [App::Part] Part015  label="Belt"
  Group = -> [Sketch005,Extrude,Sketch001,Sketch,Sketch002,Sketch003,Sketch025,Sketch008,Sketch009,Sweep003,Extrude017,Sweep,Extrude018,Sweep004,Extrude019]
  Origin = -> Origin
  Placement = pos=(0,0,-30) rot=(0,0,1;0rad)
FEATURE [Part::FeaturePython] BasePlate002  # WARN: FeaturePython — macro-defined, semantics opaque (R4)
  B = 175
  D = 19
  H = 160
  b1 = 25
  h1 = 30
  sface = 0
FEATURE [Part::Extrusion] Extrude020
  Base = -> BasePlate002
  Dir = (0,0,1)
  DirMode = 2
  FaceMakerClass = Part::FaceMakerBullseye
  LengthFwd = 10
  LengthRev = 0
  Solid = true
  Symmetric = false
FEATURE [Part::FeaturePython] Channel002  # WARN: FeaturePython — macro-defined, semantics opaque (R4)
  B = 75
  H = 150
  L = 861
  Solid = true
  g0 = 7.85
  mass = 14.5551
  size = 3
  standard = SS
  expr: L = Spreadsheet.Ht - 139
FEATURE [Part::MultiFuse] Fusion010  label="PostC003"
  Placement = pos=(0,-37.5,-861) rot=(0,0,-1;1.5708rad)
  Shapes = -> [Extrude020,Channel002]
  expr: .Placement.Base.z = -Spreadsheet.Ht + 139
FEATURE [App::Part] Part016  label="post003"
  Group = -> [BasePlate002,Channel002,Extrude020,Fusion010]
  Origin = -> Origin019
  Placement = pos=(-500,-455,-139) rot=(0,1,0;0.174533rad)
  expr: .Placement.Rotation.Angle = Spreadsheet.k
FEATURE [TechDraw::DrawSVGTemplate] Template
  Height = 420
  Orientation = 1
  Template = C:/Program Files/FreeCAD 0.21/data/Mod/TechDraw/Templates/A2_Landscape_blank.svg
  Width = 594
FEATURE [Part::FeaturePython] BasePlate003  # WARN: FeaturePython — macro-defined, semantics opaque (R4)
  B = 175
  D = 19
  H = 160
  b1 = 25
  h1 = 30
  sface = 0
FEATURE [Part::FeaturePython] Channel003  # WARN: FeaturePython — macro-defined, semantics opaque (R4)
  B = 75
  H = 150
  L = 920
  Solid = true
  g0 = 7.85
  mass = 15.5525
  size = 3
  standard = SS
FEATURE [Part::Extrusion] Extrude021
  Base = -> BasePlate003
  Dir = (0,0,1)
  DirMode = 2
  FaceMakerClass = Part::FaceMakerBullseye
  LengthFwd = 10
  LengthRev = 0
  Solid = true
  Symmetric = false
FEATURE [Part::MultiFuse] Fusion011  label="PostC004"
  Placement = pos=(0,-37.5,-861) rot=(0,0,-1;1.5708rad)
  Shapes = -> [Extrude021,Channel003]
FEATURE [App::Part] Part017  label="post004"
  Group = -> [BasePlate003,Channel003,Extrude021,Fusion011]
  Origin = -> Origin020
  Placement = pos=(550,-455,-139) rot=(0,1,0;0.174533rad)
  expr: .Placement.Rotation.Angle = Spreadsheet.k
FEATURE [App::Part] Part007  label="Post"
  Group = -> [Part016,Part017]
  Origin = -> Origin011
FEATURE [App::Part] Part002  label="600B_motorpulley"
  Group = -> [Spreadsheet,Part007,Part010,Part011,Part012,Part013,Part014,Part015]
  Origin = -> Origin007
  Placement = pos=(0,0,0) rot=(0,1,0;-0.174533rad)
  expr: .Placement.Rotation.Angle = -Spreadsheet.k
FEATURE [TechDraw::DrawViewPart] View
  CoarseView = false
  Direction = (0,-1,0)
  Focus = 100
  HardHidden = true
  IsoCount = 0
  IsoHidden = false
  IsoVisible = false
  LockPosition = false
  Perspective = false
  Rotation = 0
  Scale = 0.05
  ScaleType = 2
  ScrubCount = 0
  SeamHidden = false
  SeamVisible = false
  SmoothHidden = false
  SmoothVisible = true
  Source = -> [Part002]
  X = 297
  XDirection = (1,0,0)
  Y = 210
FEATURE [TechDraw::DrawViewDimension] Dimension
  AngleOverride = false
  Arbitrary = false
  ArbitraryTolerances = false
  EqualTolerance = true
  ExtensionAngle = 0
  FormatSpec = %.2w
  FormatSpecOverTolerance = %+.2w
  FormatSpecUnderTolerance = %+.2w
  Inverted = false
  LineAngle = 0
  LockPosition = false
  MeasureType = 1
  OverTolerance = 0
  References2D = -> [View]
  Rotation = 0
  ScaleType = 2
  TheoreticalExact = false
  Type = 2
  UnderTolerance = 0
  X = -186.785
  Y = -10.8658
FEATURE [TechDraw::DrawPage] Page
  KeepUpdated = true
  NextBalloonIndex = 1
  ProjectionType = 1
  Template = -> Template
  Views = -> [View,Dimension]
